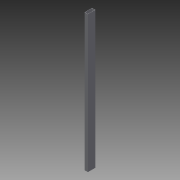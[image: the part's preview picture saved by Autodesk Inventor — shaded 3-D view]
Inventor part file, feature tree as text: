
AUTODESK INVENTOR PART (.ipt)
format: ipt  version: 2013 (Build 170138000, 138)  size: 78,848 bytes
history: native  units: in
note: dims shown in document units (in); Inventor stores cm internally (conversion verified against a paired STEP export)
features: other x2, extrude x1, sketch x1
ambient origin geometry x8: Origin, YZ Plane, XZ Plane, XY Plane, X Axis, Y Axis, Z Axis, Center Point
bodies: Solid1 (feature_tree)
feature tree (4):
  other  "Table"
  other  "squareTube1.5x2-01"
  extrude  "Extrusion1"  Depth=4.0in
  sketch  "Sketch1"  dims[d0=1.75in d1=4.0in d2=0.125in d4=0.0in]
